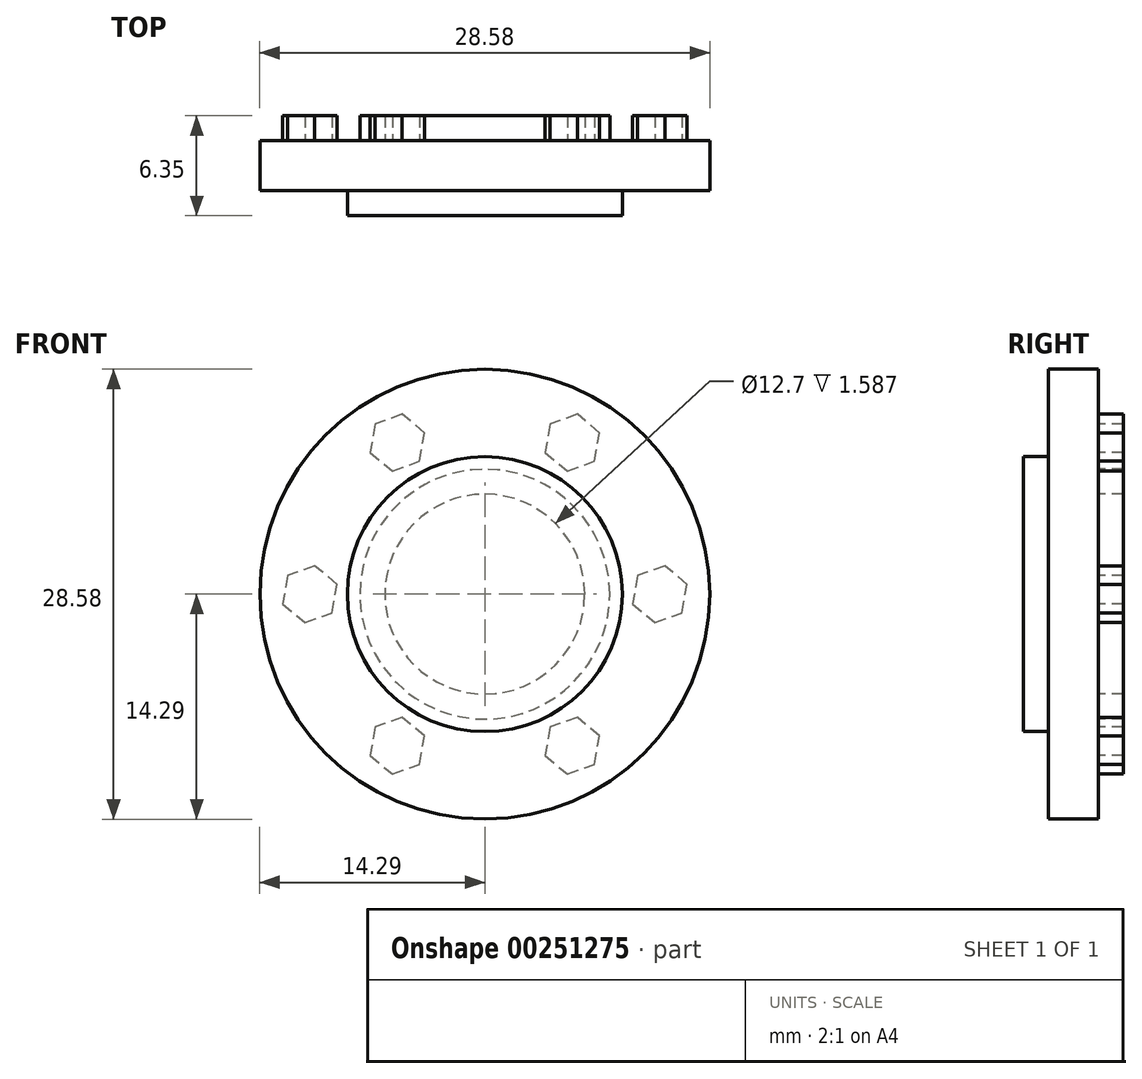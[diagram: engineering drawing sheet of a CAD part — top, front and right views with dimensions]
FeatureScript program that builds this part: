
annotation { "Feature Type Name" : "Feature", "Feature Type Description" : "" }
export const myFeature = defineFeature(function(context is Context, id is Id, definition is map)
    precondition{}
    {
        {
            var Q0;
            Q0=qCreatedBy(makeId("Front.planeOp"),FACE);
            var sketch = newSketch(context, id + "F0", { "sketchPlane" : qUnion([Q0])});
            skCircle(sketch, "E0", {"center": v(0, 0) * mm, "radius": 14.29 * mm});
            skSolve(sketch);
        }
        {
            var Q0;
            Q0 = qSketchRegion(id + "F0", true);
            extrude(context, id + "F1", {"entities" : qUnion([Q0]), "depth" : 3.17 * mm});
        }
        {
            var Q0;
            Q0=makeQuery(id+"F1.opExtrude","CAP_FACE",FACE,{"disambiguationData":[OSD([sQuery(id+"F0.wireOp",EDGE,"E0")])],"isStart":false});
            var sketch = newSketch(context, id + "F2", { "sketchPlane" : qUnion([Q0])});
            skCircle(sketch, "E1", {"center": v(0, 0) * mm, "radius": 8.73 * mm});
            skSolve(sketch);
        }
        {
            var Q0;
            Q0 = qSketchRegion(id + "F2", true);
            extrude(context, id + "F3", {"entities" : qUnion([Q0]), "operationType" : NewBodyOperationType.ADD, "depth" : 1.59 * mm});
        }
        {
            var Q0;
            Q0=makeQuery(id+"F1.opExtrude","CAP_FACE",FACE,{"disambiguationData":[OSD([sQuery(id+"F0.wireOp",EDGE,"E0")])],"isStart":true});
            var sketch = newSketch(context, id + "F4", { "sketchPlane" : qUnion([Q0])});
            skCircle(sketch, "E2.cCircle", {"center": v(11.11, 0) * mm, "radius": 1.59 * mm, "construction": true});
            skLineSegment(sketch, "E2.0", {"start": v(12.83, -0.63) * mm, "end": v(11.43, -1.8) * mm});
            skLineSegment(sketch, "E2.1", {"start": v(11.43, -1.8) * mm, "end": v(9.7, -1.18) * mm});
            skLineSegment(sketch, "E2.2", {"start": v(9.7, -1.18) * mm, "end": v(9.4, 0.63) * mm});
            skLineSegment(sketch, "E2.3", {"start": v(9.4, 0.63) * mm, "end": v(10.8, 1.8) * mm});
            skLineSegment(sketch, "E2.4", {"start": v(10.8, 1.8) * mm, "end": v(12.52, 1.18) * mm});
            skLineSegment(sketch, "E2.5", {"start": v(12.52, 1.18) * mm, "end": v(12.83, -0.63) * mm});
            skPoint(sketch, "E2.0.midPoint", {"position": v(12.13, -1.22) * mm});
            skSolve(sketch);
        }
        {
            var Q0;
            Q0 = qSketchRegion(id + "F4", true);
            extrude(context, id + "F5", {"entities" : qUnion([Q0]), "depth" : 1.59 * mm});
        }
        {
            var Q0;
            Q0=makeQuery(id+"F1.opExtrude","CAP_FACE",FACE,{"disambiguationData":[OSD([sQuery(id+"F0.wireOp",EDGE,"E0")])],"isStart":true});
            var sketch = newSketch(context, id + "F6", { "sketchPlane" : qUnion([Q0])});
            skCircle(sketch, "E3", {"center": v(0, 0) * mm, "radius": 7.94 * mm});
            skCircle(sketch, "E4", {"center": v(0, 0) * mm, "radius": 6.35 * mm});
            skSolve(sketch);
        }
        {
            var Q0;
            Q0 = qSketchRegion(id + "F6", true);
            extrude(context, id + "F7", {"entities" : qUnion([Q0]), "operationType" : NewBodyOperationType.ADD, "depth" : 1.59 * mm});
        }
        {
            var Q0;
            Q0=makeQuery(id+"F5.opExtrude","SWEPT_BODY",BODY,{"disambiguationData":[OSD([sQuery(id+"F4.wireOp",EDGE,"E2.0"),sQuery(id+"F4.wireOp",EDGE,"E2.1"),sQuery(id+"F4.wireOp",EDGE,"E2.2"),sQuery(id+"F4.wireOp",EDGE,"E2.3"),sQuery(id+"F4.wireOp",EDGE,"E2.4"),sQuery(id+"F4.wireOp",EDGE,"E2.5")])]});
            var Q1;
            Q1=makeQuery(id+"F7.opExtrude","CAP_EDGE",EDGE,{"disambiguationData":[OSD([sQuery(id+"F6.wireOp",EDGE,"E4")])],"isStart":false});
            circularPattern(context, id + "F8", {"entities" : qUnion([Q0]), "axis" : qUnion([Q1]), "angle" : 360 * degree, "instanceCount" : 6, "equalSpace" : true, "computeTransformsWithoutBuiltin" : true});
        }
    });
